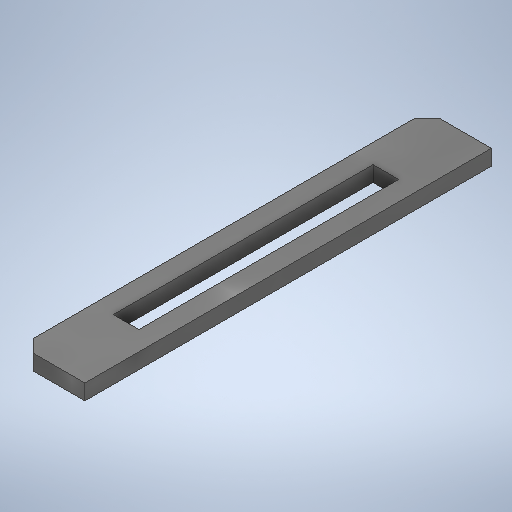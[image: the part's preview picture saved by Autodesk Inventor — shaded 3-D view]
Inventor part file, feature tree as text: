
AUTODESK INVENTOR PART (.ipt)
format: ipt  version: 2025 (Build 290162000, 162)  size: 279,040 bytes
history: native  units: in
note: dims shown in document units (in); Inventor stores cm internally (conversion verified against a paired STEP export)
features: extrude x3, sketch x3
ambient origin geometry x8: Origin, YZ Plane, XZ Plane, XY Plane, X Axis, Y Axis, Z Axis, Center Point
bodies: Solid1 (feature_tree)
feature tree (6):
  extrude  "Extrusion1"  Depth=0.0236in TaperAngle=0.0deg
  extrude  "Extrusion2"  Depth=0.3976in
  extrude  "Extrusion3"  Depth=0.0492in
  sketch  "Sketch1"  dims[d0=0.622in d1=0.0236in d2=0.0in]
  sketch  "Sketch2"  dims[d3=0.0394in d4=0.3976in]
  sketch  "Sketch3"  dims[d5=0.0in d6=0.0in d7=0.0492in d8=0.0492in d9=0.0197in d10=0.0197in d11=0.0197in d12=0.0197in d13=0.0in d14=0.0in]
